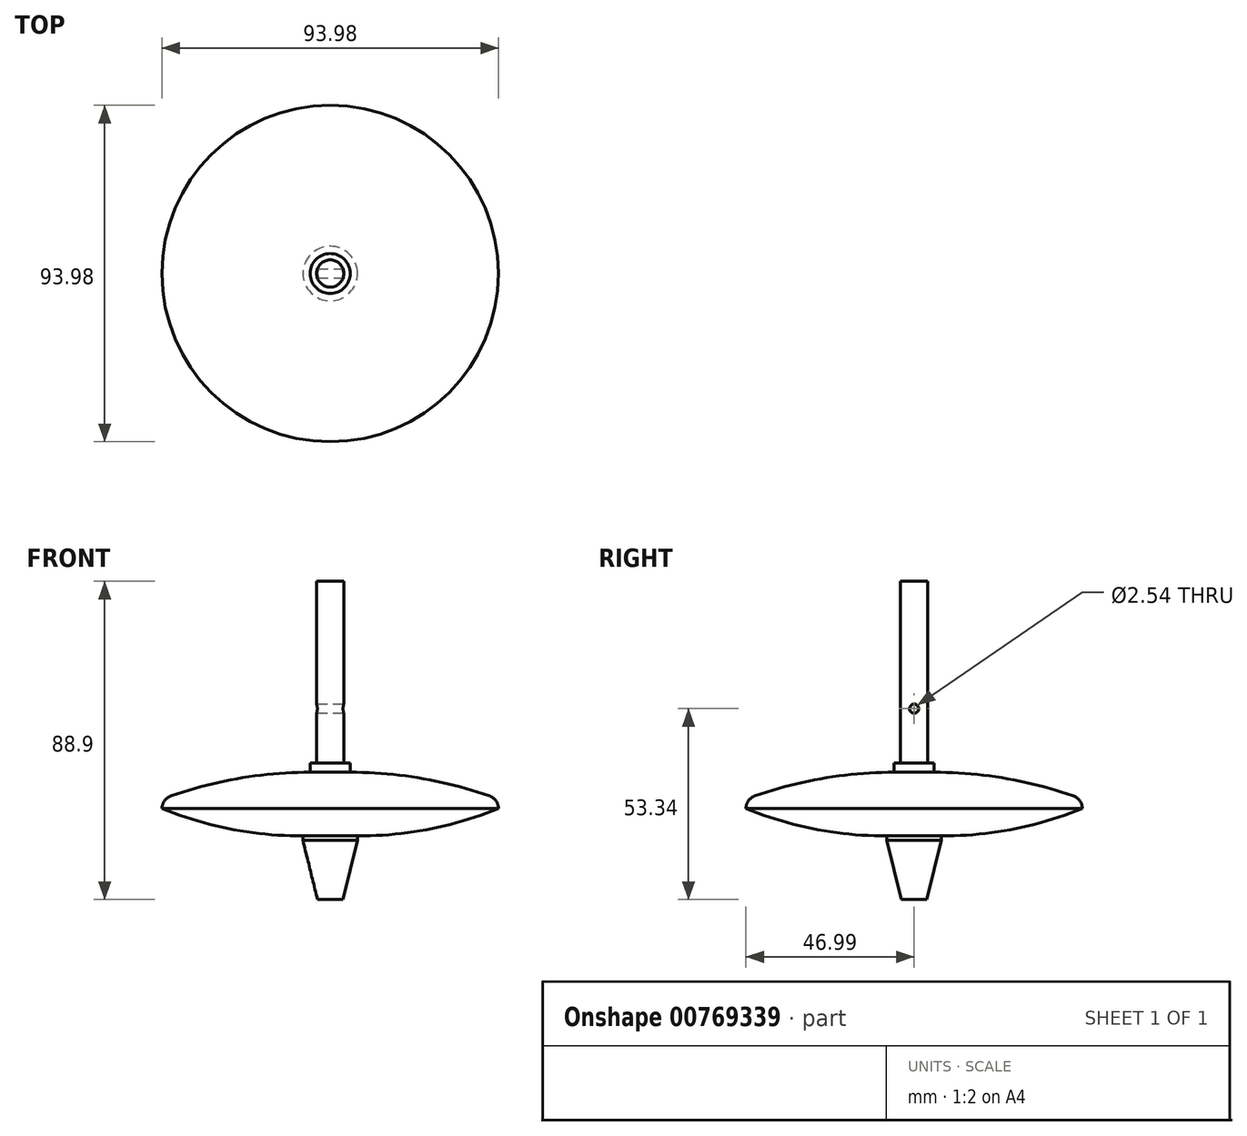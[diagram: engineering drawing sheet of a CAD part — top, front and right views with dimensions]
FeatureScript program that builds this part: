
annotation { "Feature Type Name" : "Feature", "Feature Type Description" : "" }
export const myFeature = defineFeature(function(context is Context, id is Id, definition is map)
    precondition{}
    {
        {
            var Q0;
            Q0=qCreatedBy(makeId("Front.planeOp"),FACE);
            var sketch = newSketch(context, id + "F0", { "sketchPlane" : qUnion([Q0])});
            skLineSegment(sketch, "E0", {"start": v(0, 0) * mm, "end": v(0, 88.9) * mm});
            skLineSegment(sketch, "E1", {"start": v(3.8, 88.9) * mm, "end": v(3.81, 38.1) * mm});
            skLineSegment(sketch, "E2", {"start": v(0, 88.9) * mm, "end": v(3.81, 88.9) * mm});
            skPoint(sketch, "E3.visualSharp", {"position": v(3.8, 88.9) * mm});
            skLineSegment(sketch, "E4", {"start": v(3.81, 38.1) * mm, "end": v(5.59, 38.1) * mm});
            skLineSegment(sketch, "E5", {"start": v(5.59, 38.1) * mm, "end": v(5.59, 35.56) * mm});
            skLineSegment(sketch, "E6", {"start": v(0, 0) * mm, "end": v(3.56, 0) * mm});
            skArc(sketch, "E7", {"start": v(7.62, 17.78) * mm, "mid": v(27.67, 19.7) * mm, "end": v(46.99, 25.4) * mm});
            skLineSegment(sketch, "E8", {"start": v(47, 16.23) * mm, "end": v(47, -2.45) * mm, "construction": true});
            skPoint(sketch, "E9", {"position": v(47, 6.9) * mm});
            skArc(sketch, "E10", {"start": v(47, 25.4) * mm, "mid": v(46.3, 27.6) * mm, "end": v(44.45, 28.98) * mm});
            skArc(sketch, "E11", {"start": v(44.45, 28.98) * mm, "mid": v(25.3, 33.9) * mm, "end": v(5.59, 35.56) * mm});
            skLineSegment(sketch, "E12", {"start": v(7.62, 16.51) * mm, "end": v(3.56, 0) * mm});
            skLineSegment(sketch, "E13", {"start": v(7.62, 16.51) * mm, "end": v(7.62, 17.78) * mm});
            skPoint(sketch, "E14.orphan", {"position": v(3.81, 0) * mm});
            skLineSegment(sketch, "E15", {"start": v(7.62, 17.78) * mm, "end": v(41.22, 17.78) * mm, "construction": true});
            skLineSegment(sketch, "E16", {"start": v(5.59, 35.56) * mm, "end": v(-10.23, 35.56) * mm, "construction": true});
            skPoint(sketch, "E17.visualSharp", {"position": v(3.56, 0) * mm});
            skPoint(sketch, "E18.visualSharp", {"position": v(47, 25.4) * mm});
            skSolve(sketch);
        }
        {
            var Q0;
            Q0=makeQuery(id+"F0.imprint","IMPRINT",FACE,{"disambiguationData":[TD([[makeQuery(id+"F0.imprint","IMPRINT",EDGE,{"derivedFrom":sQuery(id+"F0.wireOp",EDGE,"E0")}),-1.0]])]});
            var Q1;
            Q1=sQuery(id+"F0.wireOp",EDGE,"E0");
            revolve(context, id + "F1", {"surfaceOperationType" : NewSurfaceOperationType.NEW, "entities" : qUnion([Q0]), "axis" : qUnion([Q1]), "revolveType" : RevolveType.FULL});
        }
        {
            var Q0;
            Q0=qCreatedBy(makeId("Right.planeOp"),FACE);
            var sketch = newSketch(context, id + "F2", { "sketchPlane" : qUnion([Q0])});
            skCircle(sketch, "E19", {"center": v(0, 53.34) * mm, "radius": 1.27 * mm});
            skSolve(sketch);
        }
        {
            var Q0;
            Q0 = qSketchRegion(id + "F2", true);
            extrude(context, id + "F3", {"entities" : qUnion([Q0]), "operationType" : NewBodyOperationType.REMOVE, "oppositeDirection" : true, "depth" : 25.4 * mm, "offsetDistance" : 25.4 * mm, "symmetric" : true});
        }
    });
